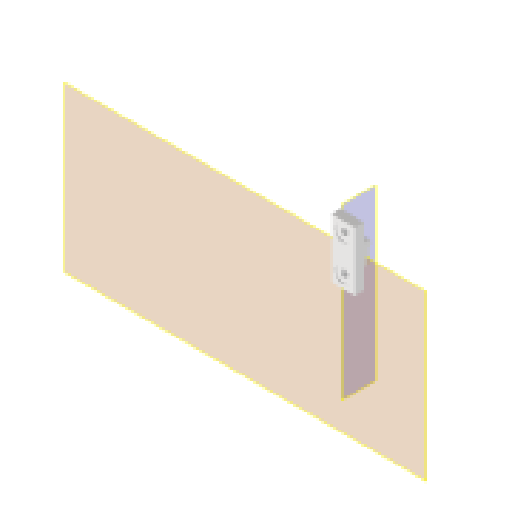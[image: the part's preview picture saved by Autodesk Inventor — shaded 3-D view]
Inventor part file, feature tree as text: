
AUTODESK INVENTOR PART (.ipt)
format: ipt  version: 2025.3 (Build 293356000, 356)  size: 123,392 bytes
history: native  units: mm
features: reference x3, plane x2, other x2, extrude x1, hole x1, fillet x1, sketch x1
ambient origin geometry x8: Origin, YZ Plane, XZ Plane, XY Plane, X Axis, Y Axis, Z Axis, Center Point
bodies: Volumenkörper1 (feature_tree)
feature tree (11):
  plane  "Arbeitsebene1"
  plane  "Arbeitsebene2"
  extrude  "Extrusion1"  Depth=1.0mm
  hole  "Bohrung1"  [1 undecoded]
  fillet  "Rundung1"  Radius=11.0mm
  sketch  "Skizze1"  dims[d0=8.0mm d1=1.0mm d2=3.5mm d3=11.0mm d4=9.0mm d5=0.0mm d6=2.8mm d7=6.0mm d8=6.5mm d9=0.5mm d10=90.0deg d11=8.0mm d12=20.594885mm d13=1.0mm d14=1.0mm]
  reference  "Referenz1"
  reference  "Referenz2"
  reference  "Referenz3"
  other  "Assembly_HoliSheet_v6.iam"
  other  "10_Wellplate_base_v6:1"
note: 1 required parameter value undecoded (feature->parameter linkage not recoverable at this tier; creation-order binding heuristic only, values carry confidence <= 0.55)
